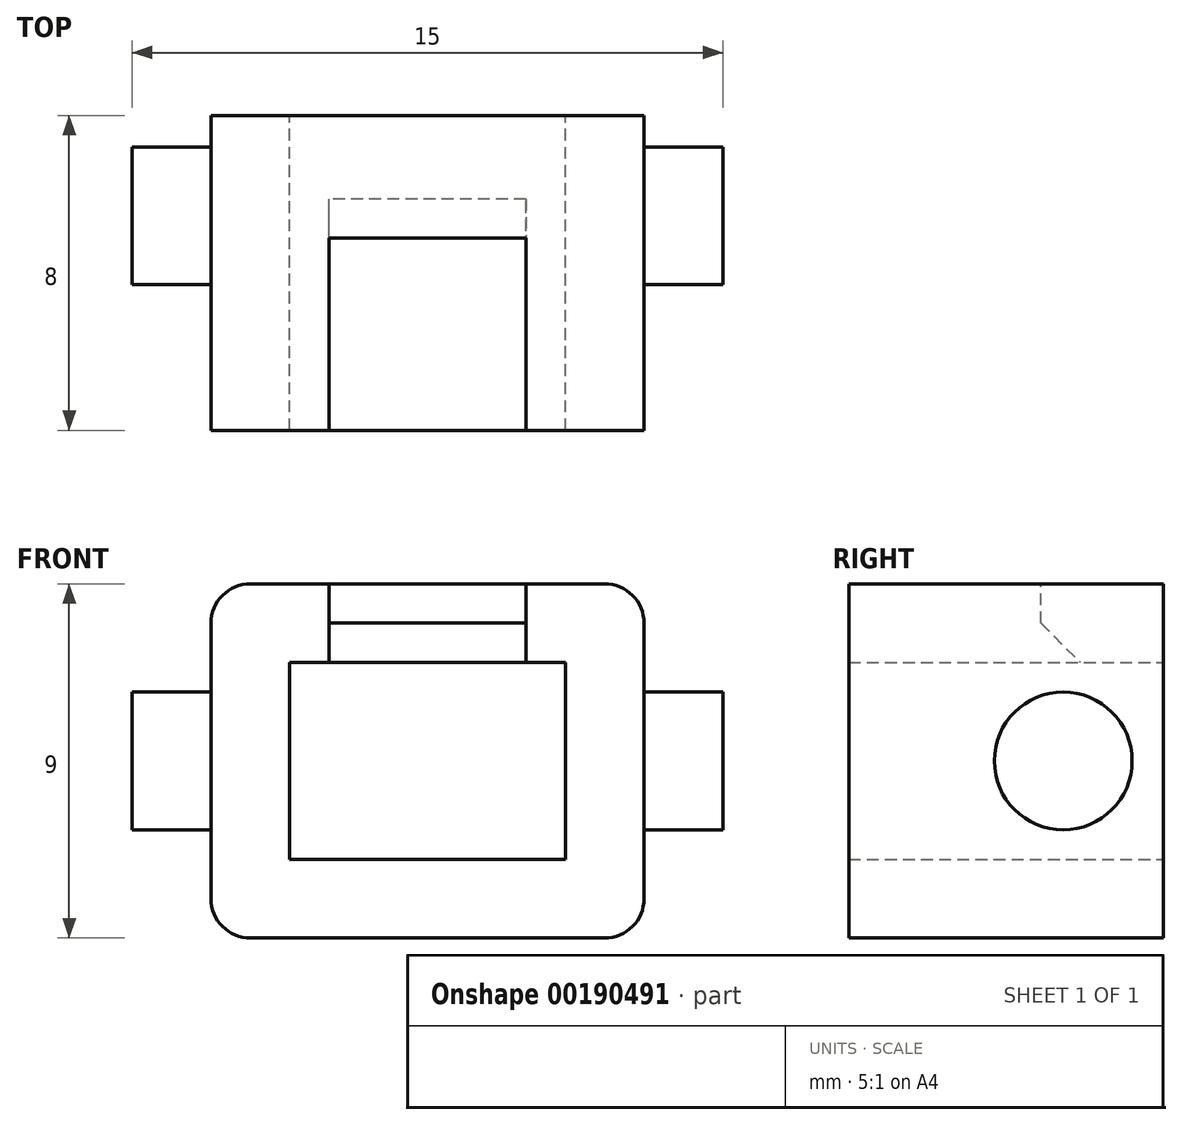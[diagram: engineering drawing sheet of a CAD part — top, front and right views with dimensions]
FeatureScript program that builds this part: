
annotation { "Feature Type Name" : "Feature", "Feature Type Description" : "" }
export const myFeature = defineFeature(function(context is Context, id is Id, definition is map)
    precondition{}
    {
        {
            var Q0;
            Q0=qCreatedBy(makeId("Front.planeOp"),FACE);
            var sketch = newSketch(context, id + "F0", { "sketchPlane" : qUnion([Q0])});
            skLineSegment(sketch, "E0.bottom", {"start": v(5.5, -4.5) * mm, "end": v(-5.5, -4.5) * mm});
            skLineSegment(sketch, "E0.top", {"start": v(5.5, 4.5) * mm, "end": v(-5.5, 4.5) * mm});
            skLineSegment(sketch, "E0.left", {"start": v(5.5, -4.5) * mm, "end": v(5.5, 4.5) * mm});
            skLineSegment(sketch, "E0.right", {"start": v(-5.5, -4.5) * mm, "end": v(-5.5, 4.5) * mm});
            skPoint(sketch, "E0.middle", {"position": v(0, 0) * mm});
            skLineSegment(sketch, "E1.0", {"start": v(-3.5, -2.5) * mm, "end": v(-3.5, 2.5) * mm});
            skLineSegment(sketch, "E1.1", {"start": v(3.5, -2.5) * mm, "end": v(-3.5, -2.5) * mm});
            skLineSegment(sketch, "E1.2", {"start": v(3.5, -2.5) * mm, "end": v(3.5, 2.5) * mm});
            skLineSegment(sketch, "E1.3", {"start": v(3.5, 2.5) * mm, "end": v(-3.5, 2.5) * mm});
            skLineSegment(sketch, "E2", {"start": v(0, 80.9) * mm, "end": v(0, -67.77) * mm, "construction": true});
            skSolve(sketch);
        }
        {
            var Q0;
            Q0=makeQuery(id+"F0.imprint","IMPRINT",FACE,{"disambiguationData":[TD([[makeQuery(id+"F0.imprint","IMPRINT",EDGE,{"derivedFrom":sQuery(id+"F0.wireOp",EDGE,"E0.bottom")}),-1.0]])]});
            extrude(context, id + "F1", {"entities" : qUnion([Q0]), "depth" : 8 * mm});
        }
        {
            var Q0;
            Q0=makeQuery(id+"F1.opExtrude","SWEPT_FACE",FACE,{"disambiguationData":[OSD([sQuery(id+"F0.wireOp",EDGE,"E0.top")])]});
            var sketch = newSketch(context, id + "F2", { "sketchPlane" : qUnion([Q0])});
            skLineSegment(sketch, "E3", {"start": v(-2.5, -3.12) * mm, "end": v(-2.5, -8) * mm});
            skLineSegment(sketch, "E4.MirrorCS", {"start": v(2.5, -3.12) * mm, "end": v(2.5, -8) * mm});
            skLineSegment(sketch, "E5", {"start": v(-2.5, -3.12) * mm, "end": v(2.5, -3.12) * mm});
            skSolve(sketch);
        }
        {
            var Q0;
            Q0 = qSketchRegion(id + "F2", true);
            var Q1;
            {var subQ0=sQuery(id+"F2.wireOp",EDGE,"E3");Q1=makeQuery(id+"F2.imprint","IMPRINT",FACE,{"disambiguationData":[TD([[makeQuery(id+"F2.imprint","IMPRINT",EDGE,{"derivedFrom":subQ0}),1.0]])]});}
            extrude(context, id + "F3", {"entities" : qUnion([Q0, Q1]), "operationType" : NewBodyOperationType.REMOVE, "oppositeDirection" : true, "depth" : 5 * mm});
        }
        {
            var Q0;
            Q0=makeQuery(id+"F1.opExtrude","SWEPT_FACE",FACE,{"disambiguationData":[OSD([sQuery(id+"F0.wireOp",EDGE,"E0.right")])]});
            var sketch = newSketch(context, id + "F4", { "sketchPlane" : qUnion([Q0])});
            skLineSegment(sketch, "E6", {"start": v(10.06, 0) * mm, "end": v(-4.73, 0) * mm, "construction": true});
            skCircle(sketch, "E7", {"center": v(2.55, 0) * mm, "radius": 1.75 * mm});
            skSolve(sketch);
        }
        {
            var Q0;
            Q0=makeQuery(id+"F4.imprint","IMPRINT",FACE,{"disambiguationData":[TD([[makeQuery(id+"F4.imprint","IMPRINT",EDGE,{"derivedFrom":sQuery(id+"F4.wireOp",EDGE,"E7")}),1.0]])]});
            extrude(context, id + "F5", {"entities" : qUnion([Q0]), "operationType" : NewBodyOperationType.ADD, "depth" : 2 * mm});
        }
        {
            var Q0;
            Q0=makeQuery(id+"F1.opExtrude","SWEPT_FACE",FACE,{"disambiguationData":[OSD([sQuery(id+"F0.wireOp",EDGE,"E0.left")])]});
            var sketch = newSketch(context, id + "F6", { "sketchPlane" : qUnion([Q0])});
            skCircle(sketch, "E8", {"center": v(-2.55, 0) * mm, "radius": 1.75 * mm});
            skSolve(sketch);
        }
        {
            var Q0;
            Q0 = qSketchRegion(id + "F6", true);
            extrude(context, id + "F7", {"entities" : qUnion([Q0]), "operationType" : NewBodyOperationType.ADD, "depth" : 2 * mm});
        }
        {
            var Q0;
            Q0=makeQuery(id+"F3.boolean.opBoolean","INTERSECT",EDGE,{"derivedFrom":[makeQuery(id+"F1.opExtrude","SWEPT_FACE",FACE,{"disambiguationData":[OSD([sQuery(id+"F0.wireOp",EDGE,"E1.3")])]}),makeQuery(id+"F3.opExtrude","SWEPT_FACE",FACE,{"disambiguationData":[OSD([sQuery(id+"F2.wireOp",EDGE,"E5")])]})]});
            chamfer(context, id + "F8", {"entities" : qUnion([Q0]), "width" : 1 * mm, "tangentPropagation" : true});
        }
        {
            var Q0;
            Q0=makeQuery(id+"F1.opExtrude","SWEPT_EDGE",EDGE,{"disambiguationData":[OSD([sQuery(id+"F0.wireOp",EDGE,"E0.top"),sQuery(id+"F0.wireOp",EDGE,"E0.left")])]});
            var Q1;
            Q1=makeQuery(id+"F1.opExtrude","SWEPT_EDGE",EDGE,{"disambiguationData":[OSD([sQuery(id+"F0.wireOp",EDGE,"E0.top"),sQuery(id+"F0.wireOp",EDGE,"E0.right")])]});
            var Q2;
            Q2=makeQuery(id+"F1.opExtrude","SWEPT_EDGE",EDGE,{"disambiguationData":[OSD([sQuery(id+"F0.wireOp",EDGE,"E0.bottom"),sQuery(id+"F0.wireOp",EDGE,"E0.left")])]});
            var Q3;
            Q3=makeQuery(id+"F1.opExtrude","SWEPT_EDGE",EDGE,{"disambiguationData":[OSD([sQuery(id+"F0.wireOp",EDGE,"E0.bottom"),sQuery(id+"F0.wireOp",EDGE,"E0.right")])]});
            fillet(context, id + "F9", {"entities" : qUnion([Q0, Q1, Q2, Q3]), "radius" : 1 * mm, "tangentPropagation" : true, "allowEdgeOverflow" : false});
        }
    });
